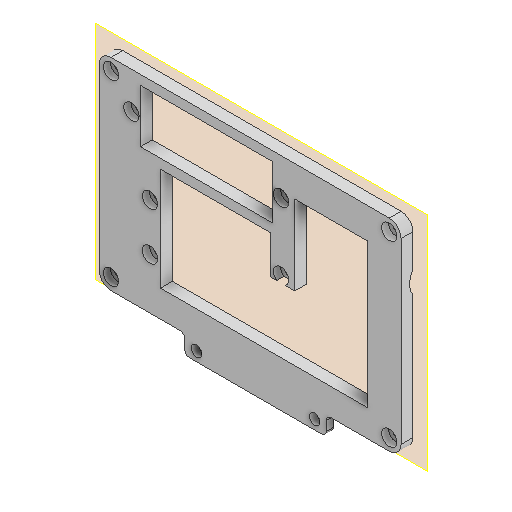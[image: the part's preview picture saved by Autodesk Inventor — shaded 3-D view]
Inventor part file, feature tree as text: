
AUTODESK INVENTOR PART (.ipt)
format: ipt  version: 2022.5 (Build 265521000, 521)  size: 269,824 bytes
history: native  units: mm
features: reference x8, extrude x5, other x5, plane x2, sketch x2, fillet x1, hole x1, projected_geometry x1
ambient origin geometry x8: Origin, YZ Plane, XZ Plane, XY Plane, X Axis, Y Axis, Z Axis, Center Point
bodies: Volumenkörper1 (feature_tree)
feature tree (25):
  plane  "Arbeitsebene1"
  extrude  "Extrusion1"  Depth=2.8mm
  extrude  "Extrusion2"  Depth=20.0mm
  fillet  "Rundung1"  Radius=5.0mm
  hole  "Bohrung1"  [1 undecoded]
  plane  "Arbeitsebene2"
  extrude  "Extrusion3"  Depth=8.0mm
  extrude  "Extrusion4"  Depth=20.0mm
  extrude  "Extrusion5"  Depth=20.0mm
  reference  "Referenz1"
  sketch  "Skizze2"  dims[d0=2.8mm d1=2.8mm]
  projected_geometry  "Projizierte Kontur1"
  reference  "Referenz2"
  reference  "Referenz3"
  reference  "Referenz4"
  sketch  "Skizze5"  dims[d2=2.8mm d3=2.8mm d4=5.0mm d5=0.0mm d6=60.0mm d7=8.0mm d8=4.5mm d9=4.5mm d10=5.0mm d11=50.0mm d12=3.0mm d13=0.0mm d14=2.0mm d15=2.9mm d16=6.0mm d17=6.5mm d18=3.0mm d19=90.0deg d20=8.0mm d21=20.594885mm d22=20.0mm d23=20.0mm d24=1.5mm d25=0.0mm d26=0.0mm d27=10.0mm d28=0.0mm d29=4.0mm d30=17.0mm d31=20.0mm d32=0.0mm]
  reference  "Referenz5"
  reference  "Referenz6"
  reference  "Referenz7"
  reference  "Referenz8"
  other  "Assembly_Guinardia_V3.iam"
  other  "10_Wellplate_base_v2:1"
  other  "Assembly_HoliSheet_v6.iam"
  other  "10_Wellplate_base_v6:1"
  other  "Assembly_Guinardia_V2.iam"
note: 1 required parameter value undecoded (feature->parameter linkage not recoverable at this tier; creation-order binding heuristic only, values carry confidence <= 0.55)
